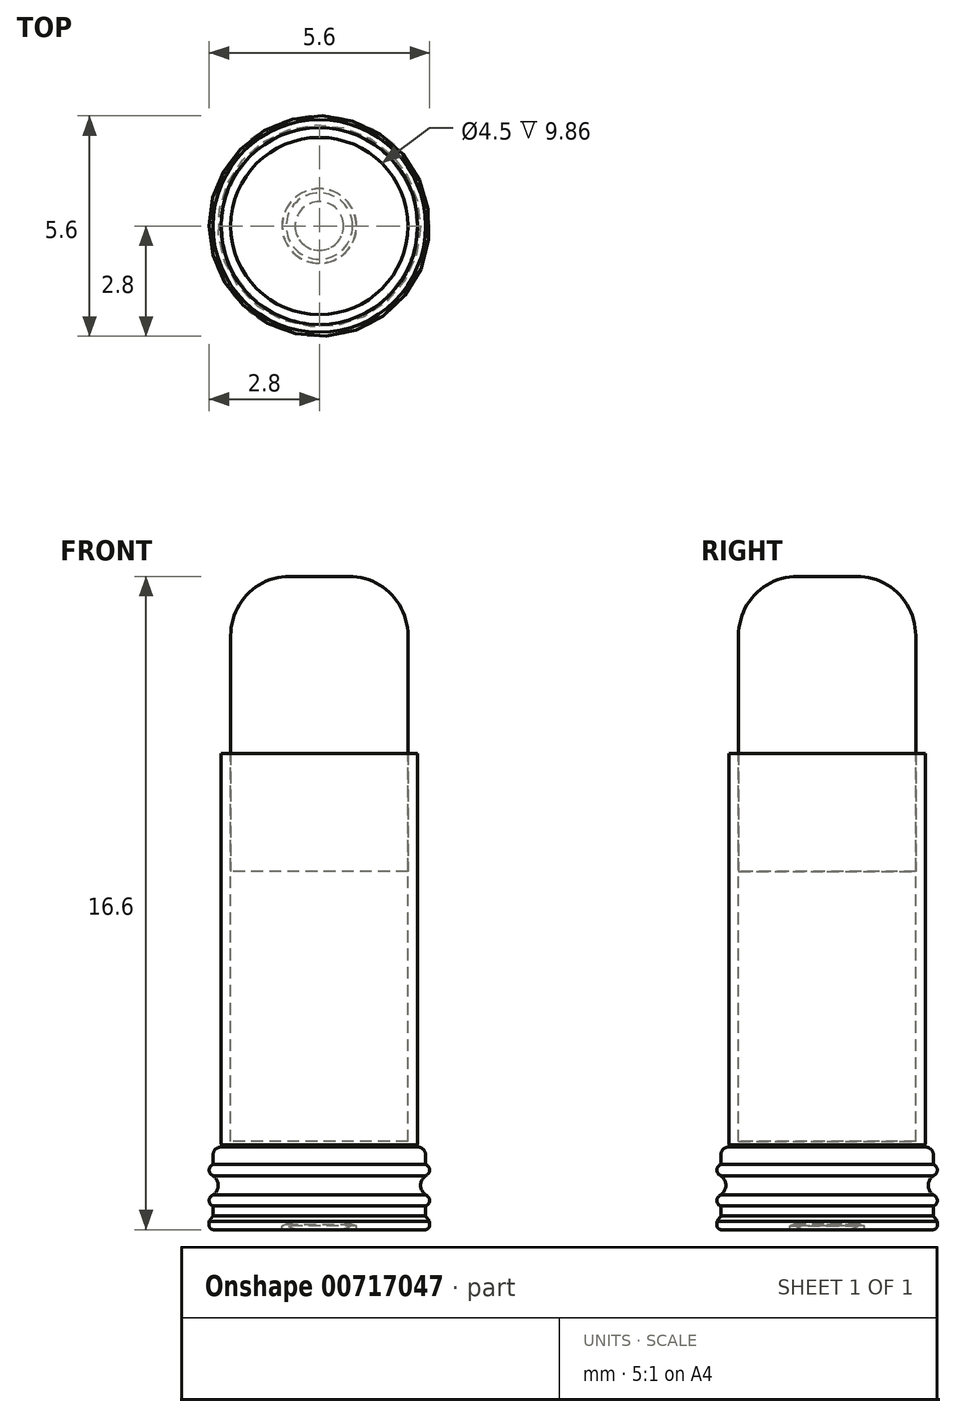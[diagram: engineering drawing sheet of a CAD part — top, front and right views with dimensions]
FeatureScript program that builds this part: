
annotation { "Feature Type Name" : "Feature", "Feature Type Description" : "" }
export const myFeature = defineFeature(function(context is Context, id is Id, definition is map)
    precondition{}
    {
        {
            var Q0;
            Q0=qCreatedBy(makeId("Top.planeOp"),FACE);
            var sketch = newSketch(context, id + "F0", { "sketchPlane" : qUnion([Q0])});
            skCircle(sketch, "E0", {"center": v(0, 0) * mm, "radius": 2.5 * mm});
            skSolve(sketch);
        }
        {
            var Q0;
            Q0 = qSketchRegion(id + "F0", true);
            extrude(context, id + "F1", {"entities" : qUnion([Q0]), "depth" : 12 * mm, "offsetDistance" : 25 * mm});
        }
        {
            var Q0;
            Q0=qCreatedBy(makeId("Front.planeOp"),FACE);
            var sketch = newSketch(context, id + "F2", { "sketchPlane" : qUnion([Q0])});
            skLineSegment(sketch, "E1", {"start": v(-2.7, 2) * mm, "end": v(-2.7, 0.25) * mm});
            skLineSegment(sketch, "E2", {"start": v(-2.7, 0.25) * mm, "end": v(-2.8, 0.11) * mm});
            skLineSegment(sketch, "E3", {"start": v(-2.8, 0.11) * mm, "end": v(-2.8, 0) * mm});
            skLineSegment(sketch, "E4", {"start": v(-2.8, 0) * mm, "end": v(-0.95, 0) * mm});
            skLineSegment(sketch, "E5", {"start": v(0, 0.1) * mm, "end": v(0, 2) * mm});
            skPoint(sketch, "E5.endSnap0", {"position": v(-2.45, 2) * mm});
            skPoint(sketch, "E6.orphan", {"position": v(-2.2, 2) * mm});
            skLineSegment(sketch, "E7", {"start": v(0, 2) * mm, "end": v(-2.7, 2) * mm});
            skLineSegment(sketch, "E8", {"start": v(-2.5, 0) * mm, "end": v(-2.5, 12) * mm, "construction": true});
            skLineSegment(sketch, "E9", {"start": v(-0.95, 0) * mm, "end": v(-0.62, 0.1) * mm});
            skLineSegment(sketch, "E10", {"start": v(-0.62, 0.1) * mm, "end": v(0, 0.1) * mm});
            skSolve(sketch);
        }
        {
            var Q0;
            Q0=makeQuery(id+"F2.imprint","IMPRINT",FACE,{"disambiguationData":[TD([[makeQuery(id+"F2.imprint","IMPRINT",EDGE,{"derivedFrom":sQuery(id+"F2.wireOp",EDGE,"E1")}),1.0]])]});
            var Q1;
            Q1=sQuery(id+"F2.wireOp",EDGE,"E5");
            revolve(context, id + "F3", {"operationType" : NewBodyOperationType.ADD, "surfaceOperationType" : NewSurfaceOperationType.NEW, "entities" : qUnion([Q0]), "axis" : qUnion([Q1]), "revolveType" : RevolveType.FULL});
        }
        {
            var Q0;
            Q0=qCreatedBy(makeId("Front.planeOp"),FACE);
            var sketch = newSketch(context, id + "F4", { "sketchPlane" : qUnion([Q0])});
            skLineSegment(sketch, "E11.0", {"start": v(-0.62, 0.1) * mm, "end": v(0, 0.1) * mm});
            skLineSegment(sketch, "E12.0", {"start": v(-0.95, 0) * mm, "end": v(-0.62, 0.1) * mm});
            skLineSegment(sketch, "E13.0", {"start": v(0, 0.1) * mm, "end": v(0, 2) * mm, "construction": true});
            skLineSegment(sketch, "E14", {"start": v(-0.95, 0) * mm, "end": v(0, 0) * mm});
            skLineSegment(sketch, "E15", {"start": v(0, 0) * mm, "end": v(0, 0.1) * mm});
            skSolve(sketch);
        }
        {
            var Q0;
            Q0 = qSketchRegion(id + "F4", true);
            var Q1;
            Q1=sQuery(id+"F2.wireOp",EDGE,"E5");
            revolve(context, id + "F5", {"operationType" : NewBodyOperationType.REMOVE, "surfaceOperationType" : NewSurfaceOperationType.NEW, "entities" : qUnion([Q0]), "axis" : qUnion([Q1]), "revolveType" : RevolveType.FULL, "oppositeDirection" : true});
        }
        {
            var Q0;
            Q0=makeQuery(id+"F3.opRevolve","SWEPT_EDGE",EDGE,{"disambiguationData":[OSD([sQuery(id+"F2.wireOp",EDGE,"E1"),sQuery(id+"F2.wireOp",EDGE,"E7")])]});
            fillet(context, id + "F6", {"entities" : qUnion([Q0]), "radius" : 0.2 * mm, "tangentPropagation" : true, "allowEdgeOverflow" : false});
        }
        {
            var Q0;
            Q0=qCreatedBy(makeId("Right.planeOp"),FACE);
            var sketch = newSketch(context, id + "F7", { "sketchPlane" : qUnion([Q0])});
            skLineSegment(sketch, "E16.0", {"start": v(2.5, 2) * mm, "end": v(-2.5, 2) * mm, "construction": true});
            skLineSegment(sketch, "E17", {"start": v(2.48, 2) * mm, "end": v(2.48, 2.05) * mm});
            skLineSegment(sketch, "E18", {"start": v(2.48, 2.05) * mm, "end": v(2.53, 2.05) * mm});
            skLineSegment(sketch, "E19", {"start": v(2.53, 2.05) * mm, "end": v(2.53, 2) * mm});
            skLineSegment(sketch, "E20", {"start": v(2.53, 2) * mm, "end": v(2.48, 2) * mm});
            skLineSegment(sketch, "E21", {"start": v(0, 1.94) * mm, "end": v(0, 2.81) * mm, "construction": true});
            skPoint(sketch, "E21.startSnap0", {"position": v(0, 2) * mm});
            skSolve(sketch);
        }
        {
            var Q0;
            Q0 = qSketchRegion(id + "F7", true);
            var Q1;
            Q1=sQuery(id+"F7.wireOp",EDGE,"E21");
            revolve(context, id + "F8", {"operationType" : NewBodyOperationType.REMOVE, "surfaceOperationType" : NewSurfaceOperationType.NEW, "entities" : qUnion([Q0]), "axis" : qUnion([Q1]), "revolveType" : RevolveType.FULL, "oppositeDirection" : true});
        }
        {
            var Q0;
            Q0=makeQuery(id+"F8.boolean.opBoolean","INTERSECT",EDGE,{"derivedFrom":[makeQuery(id+"F1.opExtrude","SWEPT_FACE",FACE,{"disambiguationData":[OSD([sQuery(id+"F0.wireOp",EDGE,"E0")])]}),makeQuery(id+"F8.opRevolve","SWEPT_FACE",FACE,{"disambiguationData":[OSD([sQuery(id+"F7.wireOp",EDGE,"E18")])]})]});
            fillet(context, id + "F9", {"entities" : qUnion([Q0]), "radius" : 0.1 * mm, "tangentPropagation" : true, "allowEdgeOverflow" : false});
        }
        {
            var Q0;
            Q0=qCreatedBy(makeId("Right.planeOp"),FACE);
            var sketch = newSketch(context, id + "F10", { "sketchPlane" : qUnion([Q0])});
            skLineSegment(sketch, "E22", {"start": v(2.7, 1.8) * mm, "end": v(2.7, 0.25) * mm});
            skPoint(sketch, "E23", {"position": v(2.7, 1.03) * mm});
            skLineSegment(sketch, "E24", {"start": v(2.7, 1.03) * mm, "end": v(3.3, 1.03) * mm, "construction": true});
            skLineSegment(sketch, "E25", {"start": v(3.3, 1.03) * mm, "end": v(3.3, 0.25) * mm, "construction": true});
            skLineSegment(sketch, "E26", {"start": v(3.3, 0.25) * mm, "end": v(2.7, 0.25) * mm, "construction": true});
            skPoint(sketch, "E27", {"position": v(3.3, 0.64) * mm});
            skLineSegment(sketch, "E28", {"start": v(3.3, 0.64) * mm, "end": v(2, 0.64) * mm, "construction": true});
            skCircle(sketch, "E29", {"center": v(2.65, 0.64) * mm, "radius": 0.15 * mm});
            skLineSegment(sketch, "E30", {"start": v(2.8, 0.11) * mm, "end": v(2.8, 0) * mm});
            skLineSegment(sketch, "E31", {"start": v(2.8, 0.11) * mm, "end": v(2.8, 1.19) * mm});
            skCircle(sketch, "E32.MirrorC", {"center": v(2.65, 1.41) * mm, "radius": 0.15 * mm});
            skLineSegment(sketch, "E33", {"start": v(0, 1.92) * mm, "end": v(0, -0.5) * mm, "construction": true});
            skSolve(sketch);
        }
        {
            var Q0;
            {var subQ0=sQuery(id+"F10.wireOp",EDGE,"E32.MirrorC");var subQ1=sQuery(id+"F10.wireOp",EDGE,"E22");var subQ2=makeQuery(id+"F10.imprint","INTERSECT",VERTEX,{"disambiguationData":[OD(0.0)],"derivedFrom":[subQ1,subQ0]});Q0=makeQuery(id+"F10.imprint","IMPRINT",FACE,{"disambiguationData":[TD([[makeQuery(id+"F10.imprint","IMPRINT",EDGE,{"disambiguationData":[TD([[subQ2,1.0]])],"derivedFrom":subQ1}),1.0]])]});}
            var Q1;
            {var subQ0=sQuery(id+"F10.wireOp",EDGE,"E29");var subQ4=makeQuery(id+"F10.imprint","IMPRINT",VERTEX,{"derivedFrom":subQ0});Q1=makeQuery(id+"F10.imprint","IMPRINT",FACE,{"disambiguationData":[TD([[makeQuery(id+"F10.imprint","IMPRINT",EDGE,{"disambiguationData":[TD([[subQ4,-1.0]])],"derivedFrom":subQ0}),1.0]])]});}
            var Q2;
            Q2=sQuery(id+"F2.wireOp",EDGE,"E5");
            revolve(context, id + "F11", {"operationType" : NewBodyOperationType.ADD, "surfaceOperationType" : NewSurfaceOperationType.NEW, "entities" : qUnion([Q0, Q1]), "axis" : qUnion([Q2]), "revolveType" : RevolveType.FULL});
        }
        {
            var Q0;
            Q0=qCreatedBy(makeId("Front.planeOp"),FACE);
            var sketch = newSketch(context, id + "F12", { "sketchPlane" : qUnion([Q0])});
            skLineSegment(sketch, "E34", {"start": v(-2.7, 0.78) * mm, "end": v(-2.7, 1.27) * mm});
            skArc(sketch, "E35", {"start": v(-2.7, 0.78) * mm, "mid": v(-2.57, 1.03) * mm, "end": v(-2.7, 1.27) * mm});
            skLineSegment(sketch, "E36", {"start": v(0, 2.6) * mm, "end": v(0, -0.5) * mm, "construction": true});
            skSolve(sketch);
        }
        {
            var Q0;
            Q0 = qSketchRegion(id + "F12", true);
            var Q1;
            Q1=sQuery(id+"F2.wireOp",EDGE,"E5");
            revolve(context, id + "F13", {"operationType" : NewBodyOperationType.REMOVE, "surfaceOperationType" : NewSurfaceOperationType.NEW, "entities" : qUnion([Q0]), "axis" : qUnion([Q1]), "revolveType" : RevolveType.FULL, "oppositeDirection" : true});
        }
        {
            var Q0;
            Q0=makeQuery(id+"F3.boolean.opBoolean","MERGE",FACE,{"derivedFrom":[makeQuery(id+"F1.opExtrude","CAP_FACE",FACE,{"disambiguationData":[OSD([sQuery(id+"F0.wireOp",EDGE,"E0")])],"isStart":true}),makeQuery(id+"F3.opRevolve","SWEPT_FACE",FACE,{"disambiguationData":[OSD([sQuery(id+"F2.wireOp",EDGE,"E4")])]})]});
            extrude(context, id + "F14", {"entities" : qUnion([Q0]), "operationType" : NewBodyOperationType.ADD, "depth" : 0.1 * mm, "offsetDistance" : 25 * mm, "hasDraft" : true, "draftAngle" : 3 * degree});
        }
        {
            var Q0;
            Q0=makeQuery(id+"F14.opExtrude","CAP_EDGE",EDGE,{"disambiguationData":[OSD([sQuery(id+"F2.wireOp",EDGE,"E3"),sQuery(id+"F2.wireOp",EDGE,"E4")])],"isStart":false});
            fillet(context, id + "F15", {"entities" : qUnion([Q0]), "radius" : 0.1 * mm, "tangentPropagation" : true, "allowEdgeOverflow" : false});
        }
        {
            var Q0;
            Q0=makeQuery(id+"F1.opExtrude","CAP_FACE",FACE,{"disambiguationData":[OSD([sQuery(id+"F0.wireOp",EDGE,"E0")])],"isStart":false});
            var sketch = newSketch(context, id + "F16", { "sketchPlane" : qUnion([Q0])});
            skCircle(sketch, "E37", {"center": v(0, 0) * mm, "radius": 2.25 * mm});
            skSolve(sketch);
        }
        {
            var Q0;
            Q0 = qSketchRegion(id + "F16", true);
            extrude(context, id + "F17", {"entities" : qUnion([Q0]), "operationType" : NewBodyOperationType.REMOVE, "oppositeDirection" : true, "depth" : 9.86 * mm, "offsetDistance" : 25 * mm});
        }
        {
            var Q0;
            Q0=makeQuery(id+"F16.imprint","IMPRINT",FACE,{"disambiguationData":[TD([[makeQuery(id+"F16.imprint","IMPRINT",EDGE,{"derivedFrom":sQuery(id+"F16.wireOp",EDGE,"E37")}),1.0]])]});
            extrude(context, id + "F18", {"entities" : qUnion([Q0]), "depth" : 4.5 * mm, "offsetDistance" : 25 * mm, "hasSecondDirection" : true, "secondDirectionOppositeDirection" : true, "secondDirectionDepth" : 3 * mm});
        }
        {
            var Q0;
            Q0=makeQuery(id+"F18.opExtrude","CAP_EDGE",EDGE,{"disambiguationData":[OSD([sQuery(id+"F16.wireOp",EDGE,"E37")])],"isStart":false});
            fillet(context, id + "F19", {"entities" : qUnion([Q0]), "radius" : 1.5 * mm, "tangentPropagation" : true, "allowEdgeOverflow" : false});
        }
        {
            var Q0;
            Q0=makeQuery(id+"F14.opExtrude","CAP_FACE",FACE,{"disambiguationData":[OSD([sQuery(id+"F0.wireOp",EDGE,"E0"),sQuery(id+"F2.wireOp",EDGE,"E4")])],"isStart":false});
            var sketch = newSketch(context, id + "F20", { "sketchPlane" : qUnion([Q0])});
            skCircle(sketch, "E38.0", {"center": v(0, 0) * mm, "radius": 0.84 * mm});
            skSolve(sketch);
        }
        {
            var Q0;
            Q0 = qSketchRegion(id + "F20", true);
            extrude(context, id + "F21", {"entities" : qUnion([Q0]), "endBound" : BoundingType.UP_TO_NEXT, "oppositeDirection" : true, "depth" : 25 * mm, "offsetDistance" : 25 * mm});
        }
        {
            var Q0;
            Q0=makeQuery(id+"F21.opExtrude","CAP_EDGE",EDGE,{"disambiguationData":[OSD([sQuery(id+"F20.wireOp",EDGE,"E38.0")])],"isStart":true});
            fillet(context, id + "F22", {"entities" : qUnion([Q0]), "radius" : 0.5 * mm, "tangentPropagation" : true, "allowEdgeOverflow" : false});
        }
    });
